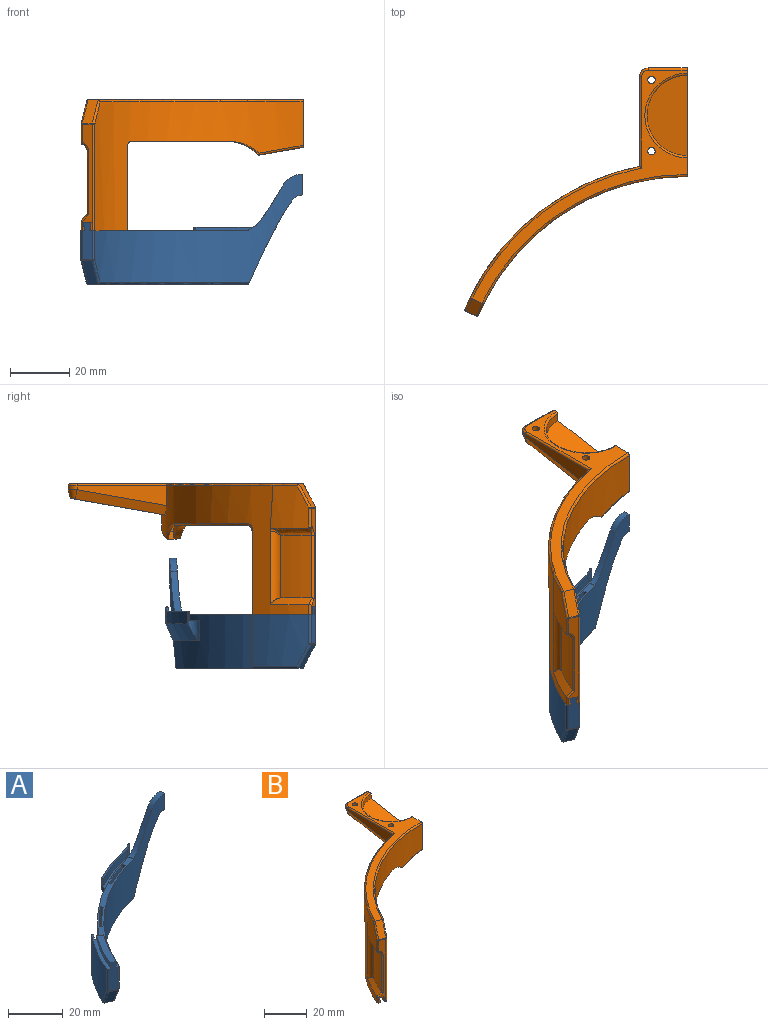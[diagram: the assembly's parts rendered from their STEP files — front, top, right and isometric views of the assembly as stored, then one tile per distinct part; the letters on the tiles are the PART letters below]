
ASSEMBLY  parts=2 mates=1
PART A: 54 faces, bbox 76.5x54.4x52.2 mm
  f0: cylinder r=76mm len=70.02mm, axis (0,0,1), area 1402.4mm2, adj f1,f2,f3,f4,f5,f6,f7,f8
  f1: extruded ~3.86x2.54mm, area 10.7mm2, adj f0,f2,f11,f12
  f2: cylinder r=4.5mm len=3.78mm, axis (0,-1,0), area 10.3mm2, adj f0,f1,f3,f12
  f3: plane 7x2.3mm, normal (1,0,0), area 16.1mm2, adj f0,f2,f4,f12
  f4: cylinder r=8mm len=7.16mm, axis (0,-1,0), area 20.4mm2, adj f0,f3,f5,f12
  f5: extruded ~14.43x11.84mm, area 43.9mm2, adj f0,f4,f6,f12
  f6: plane 2.24x0.56mm, normal (-0.97,-0.24,0), area 0.4mm2, adj f0,f5,f7,f12
  f7: plane 56.26x46.84mm, normal (0,0,1), area 162mm2, adj f0,f6,f8,f12,f13,f14,f15,f16
  f8: cylinder r=0.7mm len=9.81mm, axis (0,0,1), area 10.7mm2, adj f0,f7,f27,f31
  f9: bspline ~8.2x4.42mm, area 9.6mm2, adj f0,f10,f31,f32
  f10: torus R=76.7mm, axis (0,0,1), area 73.5mm2, adj f0,f9,f11,f16,f20,f32,f33
  f11: extruded ~24.09x12.06mm, area 65mm2, adj f0,f1,f10,f12,f33,f34,f35
  f12: cylinder r=78.3mm len=62.99mm, axis (0,0,1), area 992.9mm2, adj f1,f2,f3,f4,f5,f6,f7,f11
  f13: plane 18x0.89mm, normal (0.89,0.46,0), area 18mm2, adj f7,f14,f16,f33
  f14: cylinder r=77.7mm len=18mm, axis (0,0,1), area 232.5mm2, adj f7,f13,f15,f33
  f15: plane 18x0.95mm, normal (-0.95,-0.3,0), area 18mm2, adj f7,f14,f16,f33
  f16: cylinder r=76.7mm len=18mm, axis (0,0,1), area 229.5mm2, adj f7,f10,f13,f15
  f17: plane 18x0.74mm, normal (0.67,0.74,0), area 18mm2, adj f7,f18,f20,f33
  f18: cylinder r=77.7mm len=18mm, axis (0,0,1), area 225.5mm2, adj f7,f17,f19,f33
  f19: plane 18x0.78mm, normal (-0.78,-0.62,0), area 18mm2, adj f7,f18,f20,f33
  f20: cylinder r=76.7mm len=18mm, axis (0,0,1), area 222.6mm2, adj f7,f10,f17,f19
  f21: plane 18x1.53mm, normal (0.59,0.8,0), area 34.2mm2, adj f7,f12,f22,f33
  f22: cylinder r=80.2mm len=18mm, axis (0,0,1), area 62.8mm2, adj f7,f21,f23,f33
  f23: plane 18x0.08mm, normal (0.63,0.78,0), area 1.7mm2, adj f7,f22,f24,f33
  f24: cylinder r=0.7mm len=18mm, axis (0,0,1), area 19.6mm2, adj f7,f23,f25,f33,f39
  f25: cylinder r=81mm len=18.89mm, axis (0,0,1), area 364.6mm2, adj f7,f24,f26,f39,f40
  f26: cylinder r=0.7mm len=9.81mm, axis (0,0,1), area 10.8mm2, adj f7,f25,f27,f41
  f27: plane 12.64x3.33mm, normal (-0.38,-0.92,0), area 41.7mm2, adj f7,f8,f26,f28,f30,f42,f43
  f28: cone r=79.4mm half-angle=6.9deg, axis (0,0,1), area 51.4mm2, adj f7,f27,f29,f43
  f29: plane 2.82x2.12mm, normal (0.58,0.82,0), area 6.4mm2, adj f7,f28,f30,f43
  f30: cone r=77.2mm half-angle=6.9deg, axis (0,0,-1), area 49.9mm2, adj f7,f27,f29,f43
  f31: sphere r=0.7mm, area 0.2mm2, adj f8,f9,f42
  f32: plane 7.84x5.49mm, normal (-0.33,-0.8,-0.5), area 32.6mm2, adj f9,f10,f33,f40,f42
  f33: plane 54.01x42.72mm, normal (0,0,-1), area 114.1mm2, adj f10,f11,f12,f13,f14,f15,f17,f18
  f34: cylinder r=4mm len=5.31mm, axis (0,0,-1), area 14.6mm2, adj f11,f12,f35,f36,f44
  f35: cone r=81mm half-angle=25deg, axis (0,0,1), area 15.2mm2, adj f11,f12,f34,f38,f44,f45
  f36: plane 27.65x11.31mm, normal (0,0,1), area 47.7mm2, adj f12,f34,f37,f44,f46,f47,f48,f49
  f37: cylinder r=4mm len=6.79mm, axis (0,0,-1), area 19.2mm2, adj f12,f36,f38,f50
  f38: cone r=78.2mm half-angle=25deg, axis (0,0,1), area 139.3mm2, adj f12,f35,f37,f50,f51
  f39: torus R=80.3mm, axis (0,0,1), area 20mm2, adj f24,f25,f33,f40
  f40: bspline ~30.65x16.65mm, area 10mm2, adj f25,f32,f33,f39,f41
  f41: sphere r=0.7mm, area 0.2mm2, adj f26,f40,f42
  f42: cylinder r=0.7mm len=3.37mm, axis (0.92,-0.38,0), area 1.3mm2, adj f27,f31,f32,f41
  f43: plane 16.81x10.84mm, normal (0,0,1), area 46.3mm2, adj f27,f28,f29,f30
  f44: cylinder r=0.5mm len=6.28mm, axis (0,0,-1), area 2.9mm2, adj f34,f35,f36,f45,f46,f52
  f45: cylinder r=81mm len=5.13mm, axis (0,0,1), area 6mm2, adj f35,f44,f51,f52
  f46: cylinder r=0.5mm len=4.61mm, axis (0,0,1), area 3.8mm2, adj f36,f44,f47,f52
  f47: cylinder r=80.2mm len=4.22mm, axis (0,0,1), area 4.5mm2, adj f36,f46,f48,f52
  f48: cylinder r=80.2mm len=19.36mm, axis (0,0,-1), area 64.7mm2, adj f36,f47,f49,f53
  f49: cylinder r=0.5mm len=3.14mm, axis (0,0,-1), area 2.7mm2, adj f36,f48,f50,f53
  f50: cylinder r=0.5mm len=4.72mm, axis (0,0,-1), area 2.2mm2, adj f36,f37,f38,f49,f51,f53
  f51: cylinder r=81mm len=19.62mm, axis (0,0,-1), area 83.9mm2, adj f38,f45,f50,f53
  f52: extruded ~1.74x1.59mm, area 1.6mm2, adj f44,f45,f46,f47,f53
  f53: revolved ~20.17x7.79mm, area 17mm2, adj f48,f49,f50,f51,f52
PART B: 102 faces, bbox 98.8x99.4x66.7 mm
  f0: cylinder r=80mm len=9mm, axis (0,0,-1), area 18mm2, adj f3,f27,f29,f58
  f1: cylinder r=80mm len=45.52mm, axis (0,0,-1), area 452.5mm2, adj f27,f29,f38,f58
  f2: cylinder r=13.5mm len=27mm, axis (0,0,1), area 165mm2, adj f3,f53,f54,f66,f67,f89
  f3: plane 36.56x16.06mm, normal (1,0,0), area 132.3mm2, adj f0,f2,f4,f14,f24,f26,f27,f29
  f4: cylinder r=81mm len=74.64mm, axis (0,0,1), area 1387.6mm2, adj f3,f6,f50,f51,f64,f69,f70,f71
  f5: plane 35.81x3.33mm, normal (-0.38,-0.92,0), area 67.5mm2, adj f6,f42,f43,f45,f76,f79,f80,f83
  f6: plane 21.49x15.57mm, normal (0,0,-1), area 70mm2, adj f4,f5,f13,f14,f15,f16,f17,f18
  f7: cylinder r=77.7mm len=11mm, axis (0,0,1), area 50.3mm2, adj f8,f11,f19,f29,f36,f38
  f8: plane 10.07x0.78mm, normal (-0.78,-0.62,0), area 5.7mm2, adj f7,f11,f23,f28,f29,f36
  f9: plane 4x1.78mm, normal (0.89,0.46,0), area 4.5mm2, adj f11,f20,f22,f96,f100
  f10: plane 10.15x0.95mm, normal (-0.95,-0.3,0), area 5.1mm2, adj f20,f22,f30,f37,f46,f97
  f11: plane 35.06x24.88mm, normal (0,0,-1), area 71.7mm2, adj f7,f8,f9,f14,f16,f19,f20,f22
  f12: plane 35.68x24.2mm, normal (0,0,-1), area 4.4mm2, adj f18,f40,f47,f94
  f13: plane 28x0.08mm, normal (0.63,0.78,0), area 2.7mm2, adj f6,f18,f40,f91
  f14: cylinder r=76mm len=70.02mm, axis (0,0,1), area 1867.2mm2, adj f3,f6,f11,f15,f39,f46,f75,f78
  f15: plane 28x1.79mm, normal (0.63,0.78,0), area 64.4mm2, adj f6,f14,f16,f39
  f16: cylinder r=78.3mm len=48.35mm, axis (0,0,1), area 235.5mm2, adj f6,f11,f15,f17,f21,f25,f39,f41
  f17: plane 30x1.53mm, normal (0.59,0.8,0), area 57mm2, adj f6,f16,f18,f41
  f18: cylinder r=80.2mm len=49.52mm, axis (0,0,1), area 241.7mm2, adj f6,f12,f13,f17,f21,f25,f40,f41
  f19: plane 11x0.74mm, normal (0.67,0.74,0), area 10.3mm2, adj f7,f11,f23,f36
  f20: cylinder r=77.7mm len=11.93mm, axis (0,0,1), area 38.8mm2, adj f9,f10,f11,f46,f96
  f21: plane 2.65x1.87mm, normal (-0.98,-0.19,0), area 5mm2, adj f16,f18,f24,f48
  f22: cylinder r=76.7mm len=11.77mm, axis (0,0,1), area 102.3mm2, adj f9,f10,f11,f37,f46,f100
  f23: cylinder r=76.7mm len=9.02mm, axis (0,0,1), area 108.4mm2, adj f8,f11,f19,f36
  f24: plane 15.02x4.98mm, normal (0.17,0,-0.98), area 54mm2, adj f3,f21,f46,f47,f90,f93
  f25: plane 44.76x29.84mm, normal (0,0,-1), area 101mm2, adj f16,f18,f41,f48
  f26: plane 78.41x72.38mm, normal (0,0,1), area 478.7mm2, adj f3,f49,f59,f60,f73,f74,f75,f77
  f27: plane 57.96x28.24mm, normal (0,0,-1), area 180.7mm2, adj f0,f1,f3,f28,f30,f31,f32,f33
  f28: cylinder r=77mm len=12.75mm, axis (0,0,-1), area 86.7mm2, adj f8,f27,f29,f31,f34,f98,f101
  f29: plane 57.96x27.71mm, normal (0,0,1), area 157.7mm2, adj f0,f1,f3,f7,f8,f28,f30,f38
  f30: cylinder r=77mm len=23.35mm, axis (0,0,-1), area 214mm2, adj f3,f10,f27,f29,f32,f97
  f31: plane 0.62x0.32mm, normal (-0.89,-0.46,0), area 0mm2, adj f27,f28,f33,f98
  f32: plane 2.93x0.67mm, normal (0.95,0.3,0), area 1.7mm2, adj f27,f30,f33,f37
  f33: cylinder r=77.7mm len=11.93mm, axis (0,0,-1), area 12.6mm2, adj f27,f31,f32,f37,f98,f100
  f34: plane 2.93x0.55mm, normal (0.78,0.62,0), area 1.7mm2, adj f27,f28,f35,f36
  f35: cylinder r=77.7mm len=9.12mm, axis (0,0,-1), area 25mm2, adj f27,f34,f36,f38
  f36: torus R=79.7mm, axis (0,0,1), area 31.3mm2, adj f7,f8,f19,f23,f34,f35
  f37: torus R=79.7mm, axis (0,0,1), area 19.9mm2, adj f10,f22,f32,f33,f100
  f38: cylinder r=3mm len=9mm, axis (0,0,-1), area 36.6mm2, adj f1,f7,f27,f29,f35
  f39: cylinder r=2mm len=3.07mm, axis (-0.78,0.63,0), area 7.2mm2, adj f11,f14,f15,f16
  f40: cylinder r=2mm len=2mm, axis (-0.78,0.63,0), area 0.3mm2, adj f12,f13,f18,f92
  f41: cylinder r=2mm len=2.75mm, axis (-0.8,0.59,0), area 6mm2, adj f16,f17,f18,f25
  f42: cone r=79.47mm half-angle=6.9deg, axis (0,0,1), area 51.5mm2, adj f5,f6,f44,f45
  f43: cone r=77.13mm half-angle=6.9deg, axis (0,0,-1), area 49.9mm2, adj f5,f6,f44,f45
  f44: plane 2.82x2.23mm, normal (-0.58,-0.82,0), area 6.8mm2, adj f6,f42,f43,f45
  f45: plane 16.89x10.97mm, normal (0,0,-1), area 48.8mm2, adj f5,f42,f43,f44
  f46: bspline ~53.16x20.61mm, area 25.6mm2, adj f10,f11,f14,f16,f20,f22,f24,f90
  f47: bspline ~61x23.06mm, area 1.2mm2, adj f12,f18,f24,f93,f95
  f48: cylinder r=4mm len=4.3mm, axis (0.19,-0.98,0), area 11.9mm2, adj f16,f18,f21,f25
  f49: plane 7.84x5.49mm, normal (-0.33,-0.8,0.5), area 32.6mm2, adj f26,f75,f78,f84,f85
  f50: plane 30.1x6.61mm, normal (-1,0,0), area 119.1mm2, adj f4,f61,f64,f77
  f51: plane 32.65x15.26mm, normal (0,0.17,-0.98), area 453.2mm2, adj f3,f4,f59,f60,f62,f63,f64
  f52: plane 13x1.01mm, normal (0,1,0), area 13.1mm2, adj f3,f61,f62,f73
  f53: plane 28.52x14.81mm, normal (0,-0.17,0.98), area 295mm2, adj f2,f3,f54,f65,f66
  f54: plane 6.65x3.18mm, normal (-1,0,0), area 16.7mm2, adj f2,f53,f55,f57,f58,f65,f67
  f55: plane 6x4.43mm, normal (0,0,-1), area 10.8mm2, adj f54,f56,f58,f67
  f56: cylinder r=2.5mm len=5mm, axis (0,-1,0), area 25.4mm2, adj f55,f57,f58,f66
  f57: plane 6x4.43mm, normal (0,0,1), area 10.8mm2, adj f54,f56,f58,f65
  f58: bspline ~12.99x12.37mm, area 89mm2, adj f0,f1,f27,f29,f54,f55,f56,f57
  f59: cylinder r=1.25mm len=9.65mm, axis (0,0,1), area 74.9mm2, adj f26,f51
  f60: cylinder r=1.25mm len=5.42mm, axis (0,0,1), area 41.7mm2, adj f26,f51
  f61: cylinder r=3mm len=3mm, axis (0,0,-1), area 5.4mm2, adj f50,f52,f63,f74
  f62: plane 13x3.14mm, normal (0,0.97,-0.24), area 42.1mm2, adj f3,f51,f52,f63
  f63: bspline ~3.43x3mm, area 12.2mm2, adj f51,f61,f62,f64
  f64: plane 30.65x8.5mm, normal (-0.92,0.07,-0.38), area 106.2mm2, adj f4,f50,f51,f63
  f65: cone r=14.5mm half-angle=45deg, axis (0,0,1), area 4.3mm2, adj f53,f54,f57,f66
  f66: bspline ~7x3.87mm, area 9.3mm2, adj f2,f53,f56,f65,f67
  f67: cone r=13.5mm half-angle=45deg, axis (0,0,-1), area 8.7mm2, adj f2,f54,f55,f66
  f68: cylinder r=78.78mm len=21mm, axis (0,0,1), area 243.9mm2, adj f69,f70,f71,f83
  f69: revolved ~13.1x8.31mm, area 46.7mm2, adj f4,f68,f72,f86,f88
  f70: revolved ~13.94x8.84mm, area 43.7mm2, adj f4,f68,f71,f76,f80,f83
  f71: cylinder r=3mm len=24.72mm, axis (0,0,1), area 88.5mm2, adj f4,f68,f70,f72
  f72: bspline ~3.77x2.51mm, area 2.6mm2, adj f4,f69,f71
  f73: cylinder r=0.7mm len=13mm, axis (-1,0,0), area 14.3mm2, adj f3,f26,f52,f74
  f74: torus R=2.3mm, axis (0,0,1), area 4.7mm2, adj f26,f61,f73,f77
  f75: torus R=76.7mm, axis (0,0,1), area 93.8mm2, adj f3,f14,f26,f49,f78
  f76: cylinder r=0.7mm len=3.41mm, axis (0,0,1), area 3.7mm2, adj f4,f5,f6,f70,f80
  f77: cylinder r=0.7mm len=30.67mm, axis (0,-1,0), area 33.4mm2, adj f26,f50,f74,f81
  f78: bspline ~8.2x4.42mm, area 9.6mm2, adj f14,f49,f75,f82
  f79: cylinder r=0.7mm len=35.81mm, axis (0,0,1), area 39.1mm2, adj f5,f6,f14,f82
  f80: bspline ~12.75x11.8mm, area 3.5mm2, adj f5,f70,f76,f83
  f81: torus R=80.3mm, axis (0,0,1), area 82.1mm2, adj f4,f26,f77,f84
  f82: sphere r=0.7mm, area 0.2mm2, adj f78,f79,f85
  f83: cylinder r=0.7mm len=21.29mm, axis (0,0,1), area 23.3mm2, adj f5,f68,f70,f80,f86
  f84: bspline ~30.65x16.65mm, area 10mm2, adj f4,f26,f49,f81,f87
  f85: cylinder r=0.7mm len=3.37mm, axis (0.92,-0.38,0), area 1.3mm2, adj f5,f49,f82,f87
  f86: bspline ~3.81x2.85mm, area 4.1mm2, adj f5,f69,f83,f88
  f87: sphere r=0.7mm, area 0.2mm2, adj f84,f85,f88
  f88: cylinder r=0.7mm len=6.7mm, axis (0,0,1), area 7.2mm2, adj f4,f5,f69,f86,f87
  f89: torus R=14.2mm, axis (0,0,1), area 47.5mm2, adj f2,f3,f26
  f90: bspline ~14.94x3.32mm, area 16.1mm2, adj f3,f14,f24,f46
  f91: cylinder r=0.7mm len=28mm, axis (0,0,1), area 31mm2, adj f4,f6,f13,f92
  f92: bspline ~3.3x2.57mm, area 3.9mm2, adj f4,f40,f91,f94
  f93: bspline ~38.57x7.45mm, area 17mm2, adj f3,f4,f24,f47,f95
  f94: torus R=80.3mm, axis (0,0,1), area 48.2mm2, adj f4,f12,f92,f95
  f95: bspline ~14.29x5.91mm, area 13.4mm2, adj f4,f47,f93,f94
  f96: cone r=77.7mm half-angle=45deg, axis (0,0,1), area 19.1mm2, adj f9,f20,f29,f97
  f97: plane 1.92x1.17mm, normal (-0.67,-0.21,0.71), area 1.7mm2, adj f10,f29,f30,f96
  f98: plane 11.42x7.68mm, normal (0,0,1), area 13.7mm2, adj f28,f31,f33,f99,f100,f101
  f99: plane 8.98x8.48mm, normal (-0.46,0.89,0), area 51.8mm2, adj f29,f98,f100,f101
  f100: plane 9.16x7.51mm, normal (0.68,0.35,-0.64), area 21.4mm2, adj f9,f22,f33,f37,f98,f99
  f101: cylinder r=5mm len=8.98mm, axis (0,0,-1), area 37.4mm2, adj f28,f29,f98,f99
PLACE A t=(46.12,-60.28,18.6)mm
PLACE B t=(46.17,-60.35,18.6)mm
MATE slider B.f5 <-> A.f27  axis (-0.38,-0.92,0) through (-27.7,-50.97,-10.58)mm
